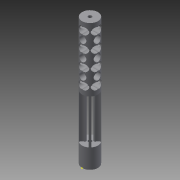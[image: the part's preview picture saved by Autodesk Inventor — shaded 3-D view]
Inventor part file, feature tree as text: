
AUTODESK INVENTOR PART (.ipt)
format: ipt  version: 2015 SP1 (Build 190203100, 203)  size: 445,952 bytes
history: native  units: in
note: dims shown in document units (in); Inventor stores cm internally (conversion verified against a paired STEP export)
features: sketch x14, extrude x11, projected_geometry x6, revolve x2, pattern_circular x1
ambient origin geometry x8: Origin, YZ Plane, XZ Plane, XY Plane, X Axis, Y Axis, Z Axis, Center Point
bodies: Solid1 (feature_tree)
feature tree (34):
  extrude  "Extrusion1"  Depth=1.0in
  extrude  "Extrusion2"  Depth=0.22in
  extrude  "Extrusion3"  Depth=0.5in
  extrude  "Extrusion4"  Depth=1.0in
  extrude  "Extrusion5"  Depth=1.75in TaperAngle=0.0deg
  extrude  "Extrusion6"  Depth=0.5in
  revolve  "Revolution1"  [1 undecoded]
  extrude  "Extrusion7"  Depth=1.0in TaperAngle=0.0deg
  extrude  "Extrusion8"  Depth=2.0in TaperAngle=0.0deg
  revolve  "Revolution2"  [1 undecoded]
  sketch  "Sketch13"  dims[d30=90.0deg d31=0.5in]
  extrude  "Extrusion9"  Depth=0.5in
  extrude  "Extrusion10"  Depth=0.5in
  sketch  "Sketch16"  dims[d40=8.0in d41=0.0in]
  pattern_circular  "Circular Pattern1"  Count=4 Angle=360.0deg
  extrude  "Extrusion11"  [1 undecoded]
  sketch  "Sketch1"  dims[d0=1.0in d1=1.0in]
  sketch  "Sketch2"  dims[d2=8.0in d3=0.0in d4=0.22in]
  sketch  "Sketch3"  dims[d5=8.9375in d6=0.0in d7=0.5in]
  projected_geometry  "Projected Loop1"
  sketch  "Sketch4"  dims[d8=1.8125in d9=0.0in d10=1.0in]
  projected_geometry  "Projected Loop2"
  sketch  "Sketch5"  dims[d11=0.44in d12=1.75in d13=0.0in]
  projected_geometry  "Projected Loop3"
  sketch  "Sketch6"  dims[d14=0.5in d15=0.44in]
  projected_geometry  "Projected Loop4"
  sketch  "Sketch7"  dims[d16=1.0625in d17=0.0in d18=0.5in]
  projected_geometry  "Projected Loop5"
  sketch  "Sketch9"  dims[d19=0.44in d20=1.0in d21=0.0in]
  sketch  "Sketch11"  dims[d22=90.0deg d23=2.0in d24=0.0in]
  sketch  "Sketch12"  dims[d27=0.5in d28=1.0in d29=0.0in]
  sketch  "Sketch14"  dims[d32=1.0in d33=0.0in d34=0.5in]
  projected_geometry  "Projected Loop9"
  sketch  "Sketch15"  dims[d35=1.0in d36=0.0in d37=1.5748in d38=360.0deg]
note: 3 required parameter values undecoded (feature->parameter linkage not recoverable at this tier; creation-order binding heuristic only, values carry confidence <= 0.55)